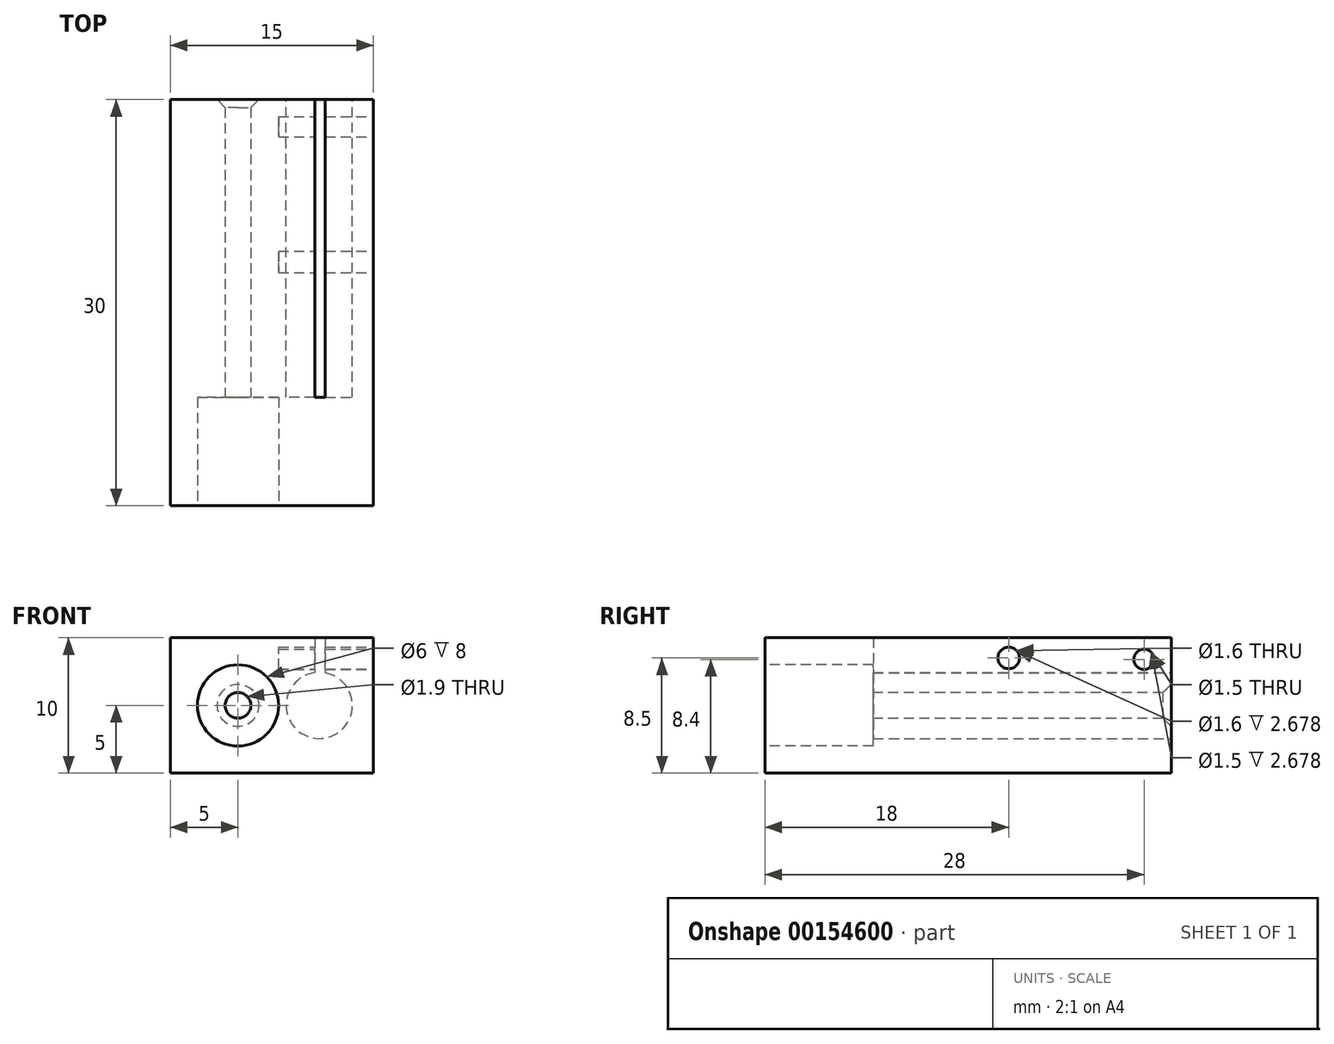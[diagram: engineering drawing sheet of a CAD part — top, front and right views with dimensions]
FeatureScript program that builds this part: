
annotation { "Feature Type Name" : "Feature", "Feature Type Description" : "" }
export const myFeature = defineFeature(function(context is Context, id is Id, definition is map)
    precondition{}
    {
        {
            var Q0;
            Q0=qCreatedBy(makeId("Top.planeOp"),FACE);
            var sketch = newSketch(context, id + "F0", { "sketchPlane" : qUnion([Q0])});
            skLineSegment(sketch, "E0.bottom", {"start": v(-7.5, 15) * mm, "end": v(7.5, 15) * mm});
            skLineSegment(sketch, "E0.top", {"start": v(-7.5, -15) * mm, "end": v(7.5, -15) * mm});
            skLineSegment(sketch, "E0.left", {"start": v(-7.5, 15) * mm, "end": v(-7.5, -15) * mm});
            skLineSegment(sketch, "E0.right", {"start": v(7.5, 15) * mm, "end": v(7.5, -15) * mm});
            skPoint(sketch, "E0.middle", {"position": v(0, 0) * mm});
            skSolve(sketch);
        }
        {
            var Q0;
            Q0=makeQuery(id+"F0.imprint","IMPRINT",FACE,{"disambiguationData":[TD([[makeQuery(id+"F0.imprint","IMPRINT",EDGE,{"derivedFrom":sQuery(id+"F0.wireOp",EDGE,"E0.bottom")}),-1.0]])]});
            extrude(context, id + "F1", {"entities" : qUnion([Q0]), "depth" : 10 * mm});
        }
        {
            var Q0;
            Q0=makeQuery(id+"F1.opExtrude","SWEPT_FACE",FACE,{"disambiguationData":[OSD([sQuery(id+"F0.wireOp",EDGE,"E0.bottom")])]});
            var sketch = newSketch(context, id + "F2", { "sketchPlane" : qUnion([Q0])});
            skCircle(sketch, "E1", {"center": v(-3.5, 5) * mm, "radius": 2.44 * mm});
            skLineSegment(sketch, "E2", {"start": v(-3.94, 10) * mm, "end": v(-3.94, 7.4) * mm});
            skLineSegment(sketch, "E3", {"start": v(-3.18, 10) * mm, "end": v(-3.18, 7.42) * mm});
            skSolve(sketch);
        }
        {
            var Q0;
            Q0=makeQuery(id+"F2.imprint","IMPRINT",FACE,{"disambiguationData":[TD([[makeQuery(id+"F2.imprint","IMPRINT",EDGE,{"derivedFrom":sQuery(id+"F2.wireOp",EDGE,"E1")}),1.0]])]});
            var Q1;
            {var subQ0=sQuery(id+"F2.wireOp",EDGE,"E2");Q1=makeQuery(id+"F2.imprint","IMPRINT",FACE,{"disambiguationData":[TD([[makeQuery(id+"F2.imprint","IMPRINT",EDGE,{"derivedFrom":subQ0}),1.0]])]});}
            extrude(context, id + "F3", {"entities" : qUnion([Q0, Q1]), "operationType" : NewBodyOperationType.REMOVE, "oppositeDirection" : true, "depth" : 22 * mm});
        }
        {
            var Q0;
            Q0=makeQuery(id+"F1.opExtrude","SWEPT_FACE",FACE,{"disambiguationData":[OSD([sQuery(id+"F0.wireOp",EDGE,"E0.right")])]});
            var sketch = newSketch(context, id + "F4", { "sketchPlane" : qUnion([Q0])});
            skCircle(sketch, "E4", {"center": v(13, 8.4) * mm, "radius": 0.75 * mm});
            skCircle(sketch, "E5", {"center": v(3, 8.5) * mm, "radius": 0.8 * mm});
            skSolve(sketch);
        }
        {
            var Q0;
            Q0 = qSketchRegion(id + "F4", true);
            extrude(context, id + "F5", {"entities" : qUnion([Q0]), "operationType" : NewBodyOperationType.REMOVE, "oppositeDirection" : true, "depth" : 7 * mm});
        }
        {
            var Q0;
            Q0=makeQuery(id+"F1.opExtrude","SWEPT_FACE",FACE,{"disambiguationData":[OSD([sQuery(id+"F0.wireOp",EDGE,"E0.top")])]});
            var sketch = newSketch(context, id + "F6", { "sketchPlane" : qUnion([Q0])});
            skCircle(sketch, "E6", {"center": v(-2.5, 5) * mm, "radius": 3 * mm});
            skSolve(sketch);
        }
        {
            var Q0;
            Q0=makeQuery(id+"F6.imprint","IMPRINT",FACE,{"disambiguationData":[TD([[makeQuery(id+"F6.imprint","IMPRINT",EDGE,{"derivedFrom":sQuery(id+"F6.wireOp",EDGE,"E6")}),1.0]])]});
            extrude(context, id + "F7", {"entities" : qUnion([Q0]), "operationType" : NewBodyOperationType.REMOVE, "oppositeDirection" : true, "depth" : 8 * mm});
        }
        {
            var Q0;
            Q0=makeQuery(id+"F7.boolean.opBoolean","COPY",FACE,{"derivedFrom":makeQuery(id+"F7.opExtrude","CAP_FACE",FACE,{"disambiguationData":[OSD([sQuery(id+"F6.wireOp",EDGE,"E6")])],"isStart":false})});
            var sketch = newSketch(context, id + "F8", { "sketchPlane" : qUnion([Q0])});
            skCircle(sketch, "E7", {"center": v(-2.5, 5) * mm, "radius": 0.95 * mm});
            skSolve(sketch);
        }
        {
            var Q0;
            Q0=makeQuery(id+"F8.imprint","IMPRINT",FACE,{"disambiguationData":[TD([[makeQuery(id+"F8.imprint","IMPRINT",EDGE,{"derivedFrom":sQuery(id+"F8.wireOp",EDGE,"E7")}),1.0]])]});
            extrude(context, id + "F9", {"entities" : qUnion([Q0]), "operationType" : NewBodyOperationType.REMOVE, "oppositeDirection" : true, "depth" : 25.4 * mm});
        }
        {
            var Q0;
            Q0=makeQuery(id+"F9.boolean.opBoolean","INTERSECT",EDGE,{"derivedFrom":[makeQuery(id+"F1.opExtrude","SWEPT_FACE",FACE,{"disambiguationData":[OSD([sQuery(id+"F0.wireOp",EDGE,"E0.bottom")])]}),makeQuery(id+"F9.opExtrude","SWEPT_FACE",FACE,{"disambiguationData":[OSD([sQuery(id+"F8.wireOp",EDGE,"E7")])]})]});
            chamfer(context, id + "F10", {"entities" : qUnion([Q0]), "width" : .6 * mm, "tangentPropagation" : true});
        }
    });
